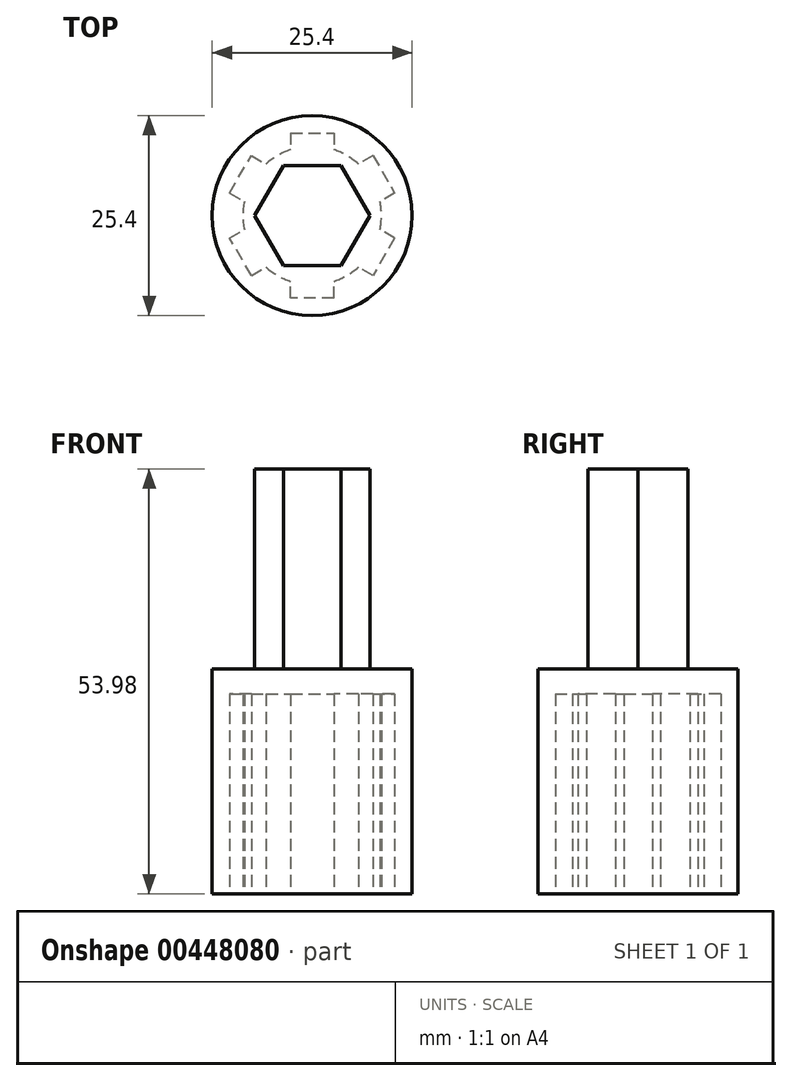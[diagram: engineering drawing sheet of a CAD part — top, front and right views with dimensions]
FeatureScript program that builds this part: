
annotation { "Feature Type Name" : "Feature", "Feature Type Description" : "" }
export const myFeature = defineFeature(function(context is Context, id is Id, definition is map)
    precondition{}
    {
        {
            var Q0;
            Q0=qCreatedBy(makeId("Top.planeOp"),FACE);
            var sketch = newSketch(context, id + "F0", { "sketchPlane" : qUnion([Q0])});
            skCircle(sketch, "E0", {"center": v(0, 0) * mm, "radius": 8.8 * mm});
            skLineSegment(sketch, "E1.bottom", {"start": v(-2.75, 10.5) * mm, "end": v(2.75, 10.5) * mm});
            skLineSegment(sketch, "E1.top", {"start": v(-2.75, 7.5) * mm, "end": v(2.75, 7.5) * mm});
            skLineSegment(sketch, "E1.left", {"start": v(-2.75, 10.5) * mm, "end": v(-2.75, 7.5) * mm});
            skLineSegment(sketch, "E1.right", {"start": v(2.75, 10.5) * mm, "end": v(2.75, 7.5) * mm});
            skPoint(sketch, "E1.middle", {"position": v(0, 9) * mm});
            skLineSegment(sketch, "E2.1.0", {"start": v(-10.47, 2.87) * mm, "end": v(-7.72, 7.63) * mm});
            skLineSegment(sketch, "E2.1.1", {"start": v(-7.72, 7.63) * mm, "end": v(-5.12, 6.13) * mm});
            skLineSegment(sketch, "E2.1.2", {"start": v(-7.87, 1.37) * mm, "end": v(-5.12, 6.13) * mm});
            skLineSegment(sketch, "E2.1.3", {"start": v(-10.47, 2.87) * mm, "end": v(-7.87, 1.37) * mm});
            skLineSegment(sketch, "E2.2.0", {"start": v(-7.72, -7.63) * mm, "end": v(-10.47, -2.87) * mm});
            skLineSegment(sketch, "E2.2.1", {"start": v(-10.47, -2.87) * mm, "end": v(-7.87, -1.37) * mm});
            skLineSegment(sketch, "E2.2.2", {"start": v(-5.12, -6.13) * mm, "end": v(-7.87, -1.37) * mm});
            skLineSegment(sketch, "E2.2.3", {"start": v(-7.72, -7.63) * mm, "end": v(-5.12, -6.13) * mm});
            skLineSegment(sketch, "E2.3.0", {"start": v(2.75, -10.5) * mm, "end": v(-2.75, -10.5) * mm});
            skLineSegment(sketch, "E2.3.1", {"start": v(-2.75, -10.5) * mm, "end": v(-2.75, -7.5) * mm});
            skLineSegment(sketch, "E2.3.2", {"start": v(2.75, -7.5) * mm, "end": v(-2.75, -7.5) * mm});
            skLineSegment(sketch, "E2.3.3", {"start": v(2.75, -10.5) * mm, "end": v(2.75, -7.5) * mm});
            skLineSegment(sketch, "E2.4.0", {"start": v(10.47, -2.87) * mm, "end": v(7.72, -7.63) * mm});
            skLineSegment(sketch, "E2.4.1", {"start": v(7.72, -7.63) * mm, "end": v(5.12, -6.13) * mm});
            skLineSegment(sketch, "E2.4.2", {"start": v(7.87, -1.37) * mm, "end": v(5.12, -6.13) * mm});
            skLineSegment(sketch, "E2.4.3", {"start": v(10.47, -2.87) * mm, "end": v(7.87, -1.37) * mm});
            skLineSegment(sketch, "E2.5.0", {"start": v(7.72, 7.63) * mm, "end": v(10.47, 2.87) * mm});
            skLineSegment(sketch, "E2.5.1", {"start": v(10.47, 2.87) * mm, "end": v(7.87, 1.37) * mm});
            skLineSegment(sketch, "E2.5.2", {"start": v(5.12, 6.13) * mm, "end": v(7.87, 1.37) * mm});
            skLineSegment(sketch, "E2.5.3", {"start": v(7.72, 7.63) * mm, "end": v(5.12, 6.13) * mm});
            skCircle(sketch, "E3", {"center": v(0, 0) * mm, "radius": 12.7 * mm});
            skSolve(sketch);
        }
        {
            var Q0;
            Q0 = qSketchRegion(id + "F0", true);
            extrude(context, id + "F1", {"entities" : qUnion([Q0]), "depth" : 25.4 * mm});
        }
        {
            var Q0;
            Q0=makeQuery(id+"F1.opExtrude","CAP_FACE",FACE,{"disambiguationData":[OSD([sQuery(id+"F0.wireOp",EDGE,"E0"),sQuery(id+"F0.wireOp",EDGE,"E1.bottom"),sQuery(id+"F0.wireOp",EDGE,"E1.left"),sQuery(id+"F0.wireOp",EDGE,"E1.right"),sQuery(id+"F0.wireOp",EDGE,"E2.1.0"),sQuery(id+"F0.wireOp",EDGE,"E2.1.1"),sQuery(id+"F0.wireOp",EDGE,"E2.1.3"),sQuery(id+"F0.wireOp",EDGE,"E2.2.0"),sQuery(id+"F0.wireOp",EDGE,"E2.2.1"),sQuery(id+"F0.wireOp",EDGE,"E2.2.3"),sQuery(id+"F0.wireOp",EDGE,"E2.3.0"),sQuery(id+"F0.wireOp",EDGE,"E2.3.1"),sQuery(id+"F0.wireOp",EDGE,"E2.3.3"),sQuery(id+"F0.wireOp",EDGE,"E2.4.0"),sQuery(id+"F0.wireOp",EDGE,"E2.4.1"),sQuery(id+"F0.wireOp",EDGE,"E2.4.3"),sQuery(id+"F0.wireOp",EDGE,"E2.5.0"),sQuery(id+"F0.wireOp",EDGE,"E2.5.1"),sQuery(id+"F0.wireOp",EDGE,"E2.5.3"),sQuery(id+"F0.wireOp",EDGE,"E3")])],"isStart":false});
            var sketch = newSketch(context, id + "F2", { "sketchPlane" : qUnion([Q0])});
            skCircle(sketch, "E4", {"center": v(0, 0) * mm, "radius": 12.7 * mm});
            skSolve(sketch);
        }
        {
            var Q0;
            Q0 = qSketchRegion(id + "F2", true);
            extrude(context, id + "F3", {"entities" : qUnion([Q0]), "operationType" : NewBodyOperationType.ADD, "depth" : 3.17 * mm});
        }
        {
            var Q0;
            Q0=makeQuery(id+"F3.opExtrude","CAP_FACE",FACE,{"disambiguationData":[OSD([sQuery(id+"F2.wireOp",EDGE,"E4")])],"isStart":false});
            var sketch = newSketch(context, id + "F4", { "sketchPlane" : qUnion([Q0])});
            skCircle(sketch, "E5.cCircle", {"center": v(0, 0) * mm, "radius": 6.35 * mm, "construction": true});
            skLineSegment(sketch, "E5.0", {"start": v(-3.67, 6.35) * mm, "end": v(3.67, 6.35) * mm});
            skLineSegment(sketch, "E5.1", {"start": v(3.67, 6.35) * mm, "end": v(7.33, 0) * mm});
            skLineSegment(sketch, "E5.2", {"start": v(7.33, 0) * mm, "end": v(3.67, -6.35) * mm});
            skLineSegment(sketch, "E5.3", {"start": v(3.67, -6.35) * mm, "end": v(-3.67, -6.35) * mm});
            skLineSegment(sketch, "E5.4", {"start": v(-3.67, -6.35) * mm, "end": v(-7.33, 0) * mm});
            skLineSegment(sketch, "E5.5", {"start": v(-7.33, 0) * mm, "end": v(-3.67, 6.35) * mm});
            skPoint(sketch, "E5.0.midPoint", {"position": v(0, 6.35) * mm});
            skSolve(sketch);
        }
        {
            var Q0;
            Q0 = qSketchRegion(id + "F4", true);
            extrude(context, id + "F5", {"entities" : qUnion([Q0]), "operationType" : NewBodyOperationType.ADD, "depth" : 25.4 * mm});
        }
    });
